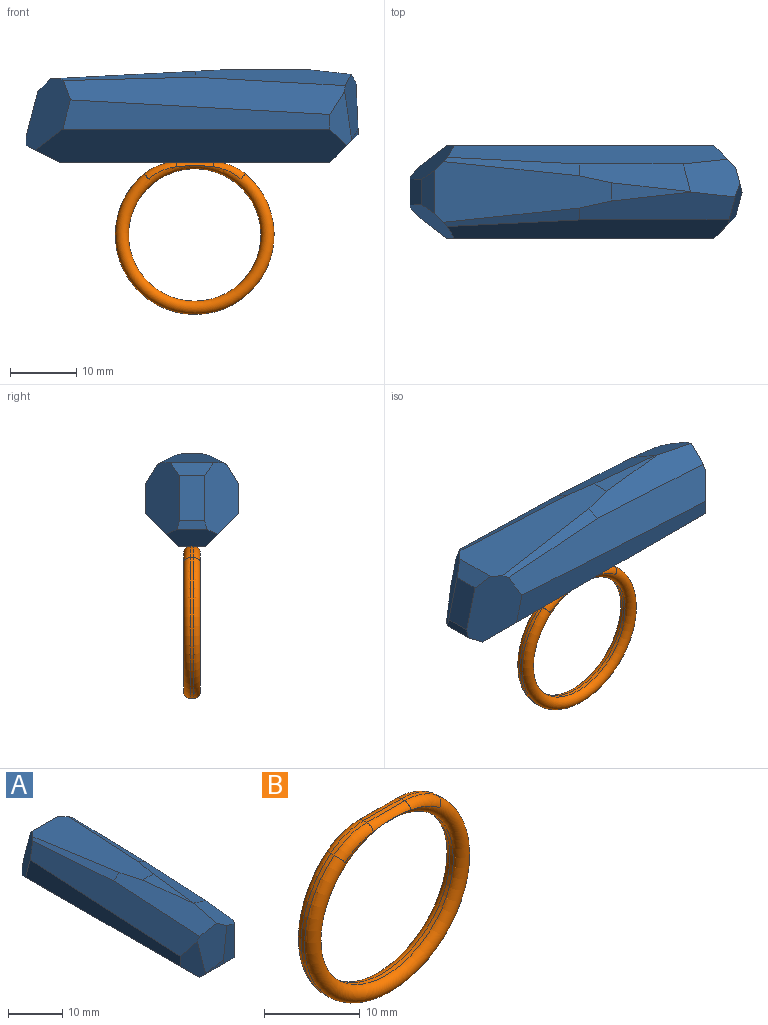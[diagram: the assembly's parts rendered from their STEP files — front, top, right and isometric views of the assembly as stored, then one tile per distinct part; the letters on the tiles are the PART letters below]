
ASSEMBLY  parts=2 mates=1
PART A: 26 faces, bbox 14x50.2x14 mm
  f0: plane 40.84x4mm, normal (0,0,-1), area 163.4mm2, adj f8,f12,f13,f16
  f1: plane 40.37x4.42mm, normal (1,0,0), area 132.9mm2, adj f6,f11,f12,f14
  f2: plane 12.11x2.75mm, normal (0,0,1), area 16.9mm2, adj f5,f20,f23,f25
  f3: plane 4.5x1.3mm, normal (0,1,0), area 5.4mm2, adj f9,f13,f14,f15
  f4: plane 20.54x2.8mm, normal (0.45,0,0.89), area 28.2mm2, adj f5,f11,f14,f23
  f5: plane 16.79x4.19mm, normal (0.45,-0.05,0.89), area 57.2mm2, adj f2,f4,f11,f23,f25
  f6: plane 8.37x3.28mm, normal (0.71,-0.71,0), area 27.7mm2, adj f1,f8,f10,f11,f12,f25
  f7: plane 6.53x1.88mm, normal (0,0.71,0.71), area 13.8mm2, adj f9,f14,f15,f23
  f8: plane 9x4.25mm, normal (0,-0.71,-0.71), area 37.2mm2, adj f0,f6,f10,f12,f16,f18,f19
  f9: plane 6.88x3.84mm, normal (0,0.97,0.25), area 27.3mm2, adj f3,f7,f14,f15
  f10: plane 8.8x3.72mm, normal (0.25,-0.97,0), area 26.1mm2, adj f6,f8,f18,f24,f25
  f11: plane 42.33x5.62mm, normal (0.85,-0.03,0.53), area 193.7mm2, adj f1,f4,f5,f6,f14,f25
  f12: plane 46.98x5mm, normal (0.71,0,-0.71), area 309.4mm2, adj f0,f1,f6,f8,f13,f14
  f13: plane 7.64x5.08mm, normal (0,0.45,-0.89), area 33.5mm2, adj f0,f3,f12,f14,f15,f16
  f14: plane 10.85x6.71mm, normal (0.71,0.68,0.18), area 64.8mm2, adj f1,f3,f4,f7,f9,f11,f12,f13
  f15: plane 10.85x6.71mm, normal (-0.71,0.68,0.18), area 64.8mm2, adj f3,f7,f9,f13,f16,f17,f21,f22
  f16: plane 46.98x5mm, normal (-0.71,0,-0.71), area 309.4mm2, adj f0,f8,f13,f15,f19,f22
  f17: plane 42.58x5.62mm, normal (-0.85,-0.03,0.53), area 198.5mm2, adj f15,f19,f20,f21,f22,f24
  f18: plane 3.72x1.88mm, normal (-0.25,-0.97,0), area 1.9mm2, adj f8,f10,f19,f24
  f19: plane 8.21x3.28mm, normal (-0.71,-0.71,0), area 22.3mm2, adj f8,f16,f17,f18,f22,f24
  f20: plane 23.53x4.21mm, normal (-0.45,-0.05,0.89), area 87mm2, adj f2,f17,f21,f23,f24,f25
  f21: plane 20.54x2.8mm, normal (-0.45,0,0.89), area 28.2mm2, adj f15,f17,f20,f23
  f22: plane 40.37x4.42mm, normal (-1,0,0), area 132.9mm2, adj f15,f16,f17,f19
  f23: plane 26.8x9.17mm, normal (0,0.05,1), area 173.8mm2, adj f2,f4,f5,f7,f14,f15,f20,f21
  f24: plane 9.9x5.98mm, normal (-0.29,-0.95,0.09), area 42.5mm2, adj f10,f17,f18,f19,f20,f25
  f25: plane 8.56x5.72mm, normal (0.46,-0.15,0.87), area 43.2mm2, adj f2,f5,f6,f10,f11,f20,f24
PART B: 13 faces, bbox 26x2.5x26 mm
  f0: plane 5.57x0.5mm, normal (0,0,1), area 2.8mm2, adj f3,f4,f8,f12
  f1: cylinder r=10mm len=20mm, axis (0,1,0), area 31.4mm2, adj f5,f9
  f2: cylinder r=12mm len=24mm, axis (0,1,0), area 29.4mm2, adj f3,f4,f5,f9
  f3: cylinder r=7.62mm len=4.85mm, axis (0,1,0), area 2.6mm2, adj f0,f2,f7,f10
  f4: cylinder r=7.62mm len=4.85mm, axis (0,1,0), area 2.6mm2, adj f0,f2,f6,f11
  f5: torus R=11mm, axis (0,-1,0), area 187.9mm2, adj f1,f2,f6,f7,f8
  f6: torus R=6.62mm, axis (0,-1,0), area 7.1mm2, adj f4,f5,f8
  f7: torus R=6.62mm, axis (0,-1,0), area 7.1mm2, adj f3,f5,f8
  f8: cylinder r=1mm len=5.57mm, axis (1,0,0), area 6.2mm2, adj f0,f5,f6,f7
  f9: torus R=11mm, axis (0,-1,0), area 187.9mm2, adj f1,f2,f10,f11,f12
  f10: torus R=6.62mm, axis (0,-1,0), area 7.1mm2, adj f3,f9,f12
  f11: torus R=6.62mm, axis (0,-1,0), area 7.1mm2, adj f4,f9,f12
  f12: cylinder r=1mm len=5.57mm, axis (-1,0,0), area 6.2mm2, adj f0,f9,f10,f11
PLACE A rot(axis=(0,0,1),90deg) t=(4.38,1.04,16.7)mm
PLACE B t=(3.88,2.29,-1.3)mm
MATE fastened A.f0 <-> B.f0  axis (0,0,-1) through (3.88,1.04,9.7)mm
